# Revit family: FT Watex 2LED MODULES_2020
name_source: partatom
category: Lighting Fixtures
units: mm (PartAtom-declared; Revit-internal decimal feet)

## family parameters
Always vertical = Yes
Cut with Voids When Loaded = No
Light Source = Yes
OmniClass Number = 23.80.70.00
OmniClass Title = Lighting
Part Type = Normal
Room Calculation Point = No
Round Connector Dimension = Use Diameter
Shared = No
Work Plane-Based = No

## types (12) — shared parameters
C = 100 mm  [stored 0.328084 ft]
Color Filter = 16777215
D = 110 mm  [stored 0.360892 ft]
Description = https://www.airfal.com
Dimming Lamp Color Temperature Shift = <None>
EX Area = II 3GD Ex nR IIC T5 Gc Ex tb IIIC T100°C Dc
Emergency system = No
Emit from Line Length = 610 mm
IK = IK08
IP = IP66
Led Module = Yes
URL = https://www.airfal.com
Useful life = L70B50>50000
zero-valued in all types: Default Elevation

## per-type parameters (varying)
| type | A (Housing) | B | L | L1 (diffuser) | Net output | Photometric Web File | Tilt Angle | Watts | l (plate) |
| EY113 | 664 mm  [stored 2.17848 ft] | 260 mm  [stored 0.853018 ft] | 600 mm  [stored 1.9685 ft] | 660 mm | 2420 lm | EY113 24W 2980 lm.IES | 90.00° | 24 W | 629 mm |
| EY114 | 664 mm  [stored 2.17848 ft] | 260 mm  [stored 0.853018 ft] | 600 mm  [stored 1.9685 ft] | 660 mm | 2598 lm | EY114 24W 3200 lm.IES | 90.00° | 24 W | 629 mm |
| EY123 | 664 mm  [stored 2.17848 ft] | 260 mm  [stored 0.853018 ft] | 600 mm  [stored 1.9685 ft] | 660 mm | 4157 lm | EY123 32W 5120 lm.IES | 90.00° | 32 W | 629 mm |
| EY124 | 664 mm  [stored 2.17848 ft] | 260 mm  [stored 0.853018 ft] | 600 mm  [stored 1.9685 ft] | 660 mm | 5340 lm | EY124 32W 5340 lm.IES | 90.00° | 32 W | 629 mm |
| EY213 | 1274 mm  [stored 4.17979 ft] | 870 mm  [stored 2.85433 ft] | 1200 mm | 1268 mm | 4840 lm | EY213 48W 5960 lm.IES | 90.00° | 48 W | 1274 mm  [stored 4.17979 ft] |
| EY214 | 1274 mm  [stored 4.17979 ft] | 870 mm  [stored 2.85433 ft] | 1200 mm | 1268 mm | 5197 lm | EY214 48W 6400 lm.IES | 90.00° | 48 W | 1240 mm  [stored 4.06824 ft] |
| EY223 | 1274 mm  [stored 4.17979 ft] | 870 mm  [stored 2.85433 ft] | 1200 mm | 1268 mm | 8315 lm | EY223 64W 10240 lm.IES | 90.00° | 64 W | 1240 mm  [stored 4.06824 ft] |
| EY224 | 1274 mm  [stored 4.17979 ft] | 870 mm  [stored 2.85433 ft] | 1200 mm | 1268 mm | 8672 lm | generic | 60.00° | 64 W | 1240 mm  [stored 4.06824 ft] |
| EY313 | 1575 mm  [stored 5.16732 ft] | 642 mm | 1500 mm  [stored 4.92126 ft] | 1568 mm  [stored 5.14436 ft] | 6041 lm | EY313 58W 7440 lm.IES | 90.00° | 58 W | 1541 mm  [stored 5.05577 ft] |
| EY314 | 1575 mm  [stored 5.16732 ft] | 650 mm  [stored 2.13255 ft] | 1500 mm  [stored 4.92126 ft] | 1568 mm  [stored 5.14436 ft] | 6496 lm | EY314 58W 8000 lm.IES | 90.00° | 58 W | 1541 mm  [stored 5.05577 ft] |
| EY323 | 1575 mm  [stored 5.16732 ft] | 650 mm  [stored 2.13255 ft] | 1500 mm  [stored 4.92126 ft] | 1568 mm  [stored 5.14436 ft] | 10247 lm | EY323 80W 12620 lm.IES | 90.00° | 80 W | 1541 mm  [stored 5.05577 ft] |
| EY324 | 1575 mm  [stored 5.16732 ft] | 650 mm  [stored 2.13255 ft] | 1500 mm  [stored 4.92126 ft] | 1568 mm  [stored 5.14436 ft] | 10881 lm | EY324 80W 13400 lm.IES | 90.00° | 80 W | 1541 mm  [stored 5.05577 ft] |

note: [stored X ft] marks values corroborated as IEEE doubles in the binary element streams (Revit-internal decimal feet)

## geometry (parser evidence)
native form markers: Blend x2, Sweep x10
no freeform markers — native parametric forms only
